# Revit family: Multibrand_Prosys_R0096_BIM_NN
name_source: partatom
category: Plumbing Fixtures
revit_build: Autodesk Revit 2017 (Build: 20160225_1515(x64)
units: mm (PartAtom-declared; Revit-internal decimal feet)

## family parameters
Cut with Voids When Loaded = No
Host = Face
OmniClass Number = 23.45.05.21.11.11
OmniClass Title = Water Operated Water Closets
Part Type = Normal
Room Calculation Point = No
Round Connector Dimension = Use Diameter
Shared = Yes

## types (1)
- R009667 - Prosys 1100 Dry WC 120 self standing CL1(NF)Pneumatic
    Accessories = www.idealspec.co.uk
    AreaUnits = millimeters
    Assembly Code = C1030200
    AssetType = Fixed
    BIMObjectName = Multibrand_Porcher_WC cistern fittings_Prosys_R009667
    BREEAMApproved = No
    BarCode = 3391500579552
    Brand = Porcher
    CWFU = 0
    ConnectionType = Plumbing
    Cost = 0 $
    Default Elevation = 0 mm  [stored 0 ft]
    Description = 1100 Dry WC 120 self standing CL1(NF)Pneumatic
    DurationUnit = year
    ECA = No
    Finish = Black/Blue
    HWFU = 0
    Help = www.idealspec.co.uk/contact-us.html
    IfcExportAs = IfcSanitaryTerminalType
    IfcExportType = CISTERN
    InstallationInstructions = www.idealspec.co.uk/resources.html
    LinearUnits = millimeters
    ManufacturerURL = www.idealspec.co.uk
    Model = R009667
    ModelNumber = R009667
    ModelReference = 1100 Dry WC 120 self standing CL1(NF)Pneumatic
    NBSDescription = WC cistern fittings
    NBSReference = 45-30-70/387
    Name = WC cistern fittings_Prosys_R009667_Porcher
    NominalDepth = 122 mm
    NominalHeight = 1134 mm
    NominalLength = 122 mm
    NominalWidth = 500 mm  [stored 1.64042 ft]
    ProductInformation = www.idealspec.co.uk/assets/datasheet/R009667
    Shape = Sculptured
    Size = 500 x 122 x 1134  mm
    Space = Internal
    SpilloverLevel = 0 mm  [stored 0 ft]
    ToiletPanType = WashDown
    ToiletType = Other
    URL = www.idealspec.co.uk
    Uniclass2 = Pr_40_20_93_89
    Uniclass2015Code = Pr_40_20_93_89
    Uniclass2015Description = WC cisterns
    Uniclass2015Version = 1
    Version = 1
    VolumeUnits = Litres
    WFU = 0
    WRAS = No
    WarrantyDescription = Manufacturers Warranty
    WarrantyDurationParts = 0
    WarrantyDurationUnit = year
    WaterEfficientProduct = No

note: [stored X ft] marks values corroborated as IEEE doubles in the binary element streams (Revit-internal decimal feet)

## geometry (parser evidence)
native form markers: Sweep x4
no freeform markers — native parametric forms only
